# Revit family: CA-4_DWDI_ARR_3_CCW_BHD
name_source: partatom
category: Mechanical Equipment
units: mm (PartAtom-declared; Revit-internal decimal feet)

## family parameters
Always vertical = Yes
Cut with Voids When Loaded = No
Part Type = Normal
Room Calculation Point = No
Round Connector Dimension = Use Radius
Shared = No
Work Plane-Based = No

## types (54) — shared parameters
0 = 0"
1" = 1"
1.5 = 1 1/2"
2" = 2"
2' = 24"
3" = 3"
4" = 4"
Manufacturer = Loren Cook Company
ONE EIGTH = 1/8"
Type Comments = Airfoil Centrifugal Blower Arrangement 3 Counter-Clockwise Bottom Horizontal Discharge
URL = www.lorencook.com

## per-type parameters (varying)
- 120_CA-4_DWDI_ARR_3_CCW_BHD_CLASS_1: (B/2)+J=10 27/32"; (F/2)-S=3 7/8"; -(B/2)-J=-10 27/32"; -B=-17 11/16"; -B/2=-8 27/32"; -J*1.5=-3"; -L+M=-22 15/16"; -M=-5 3/4"; A=12 1/8"; A+.25"=12 3/8"; B=17 11/16"; B+.25"=17 15/16"; B/2=8 27/32"; BHD_E=10 3/4"; D=25 15/16"; D/2=12 31/32"; E=15 3/16"; E+(INLET_RAD+1.5")=24 13/16"; E-(INLET_RAD+1.5")=5 9/16"; F=22 3/4"; F/2=11 3/8"; F/8=2 27/32"; G=10 3/8"; H=2"; INLET_DIA=16 1/4"; INLET_RAD=8 1/8"; INLET_RAD+1.5"=9 5/8"; INLET_RAD/2=4 1/16"; J=2"; J*1.5=3"; J-.125"=1 7/8"; L=28 11/16"; M=5 3/4"; Model=CA-4 DWDI CCW BHD Class 1; N=1 7/16"; N*2=2 7/8"; N/2=23/32"; O=9 31/32"; P=19 15/16"; P/2=9 31/32"; S=7 1/2"; T=11/16"; T/2=11/32"
- 120_CA-4_DWDI_ARR_3_CCW_BHD_CLASS_2: (B/2)+J=10 27/32"; (F/2)-S=3 7/8"; -(B/2)-J=-10 27/32"; -B=-17 11/16"; -B/2=-8 27/32"; -J*1.5=-3"; -L+M=-23 5/16"; -M=-6 1/8"; A=12 1/8"; A+.25"=12 3/8"; B=17 11/16"; B+.25"=17 15/16"; B/2=8 27/32"; BHD_E=10 3/4"; D=25 15/16"; D/2=12 31/32"; E=15 3/16"; E+(INLET_RAD+1.5")=24 13/16"; E-(INLET_RAD+1.5")=5 9/16"; F=22 3/4"; F/2=11 3/8"; F/8=2 27/32"; G=10 3/8"; H=2"; INLET_DIA=16 1/4"; INLET_RAD=8 1/8"; INLET_RAD+1.5"=9 5/8"; INLET_RAD/2=4 1/16"; J=2"; J*1.5=3"; J-.125"=1 7/8"; L=29 7/16"; M=6 1/8"; Model=CA-4 DWDI CCW BHD Class 2; N=1 11/16"; N*2=3 3/8"; N/2=27/32"; O=9 31/32"; P=19 15/16"; P/2=9 31/32"; S=7 1/2"; T=11/16"; T/2=11/32"
- 120_CA-4_DWDI_ARR_3_CCW_BHD_CLASS_3: (B/2)+J=10 27/32"; (F/2)-S=3 7/8"; -(B/2)-J=-10 27/32"; -B=-17 11/16"; -B/2=-8 27/32"; -J*1.5=-3"; -L+M=-23 9/16"; -M=-6 3/8"; A=12 1/8"; A+.25"=12 3/8"; B=17 11/16"; B+.25"=17 15/16"; B/2=8 27/32"; BHD_E=10 3/4"; D=25 15/16"; D/2=12 31/32"; E=15 3/16"; E+(INLET_RAD+1.5")=24 13/16"; E-(INLET_RAD+1.5")=5 9/16"; F=22 3/4"; F/2=11 3/8"; F/8=2 27/32"; G=10 3/8"; H=2"; INLET_DIA=16 1/4"; INLET_RAD=8 1/8"; INLET_RAD+1.5"=9 5/8"; INLET_RAD/2=4 1/16"; J=2"; J*1.5=3"; J-.125"=1 7/8"; L=29 15/16"; M=6 3/8"; Model=CA-4 DWDI CCW BHD Class 3; N=1 15/16"; N*2=3 7/8"; N/2=31/32"; O=9 31/32"; P=19 15/16"; P/2=9 31/32"; S=7 1/2"; T=11/16"; T/2=11/32"
- 135_CA-4_DWDI_ARR_3_CCW_BHD_CLASS_1: (B/2)+J=11 31/32"; (F/2)-S=4 1/4"; -(B/2)-J=-11 31/32"; -B=-19 15/16"; -B/2=-9 31/32"; -J*1.5=-3"; -L+M=-25 3/16"; -M=-5 3/4"; A=13 5/8"; A+.25"=13 7/8"; B=19 15/16"; B+.25"=20 3/16"; B/2=9 31/32"; BHD_E=12"; D=28 13/16"; D/2=14 13/32"; E=16 13/16"; E+(INLET_RAD+1.5")=27 3/16"; E-(INLET_RAD+1.5")=6 7/16"; F=25 1/2"; F/2=12 3/4"; F/8=3 3/16"; G=11 5/8"; H=2"; INLET_DIA=17 3/4"; INLET_RAD=8 7/8"; INLET_RAD+1.5"=10 3/8"; INLET_RAD/2=4 7/16"; J=2"; J*1.5=3"; J-.125"=1 7/8"; L=30 15/16"; M=5 3/4"; Model=CA-4 DWDI CCW BHD Class 1; N=1 7/16"; N*2=2 7/8"; N/2=23/32"; O=11 3/32"; P=22 3/16"; P/2=11 3/32"; S=8 1/2"; T=11/16"; T/2=11/32"
- 135_CA-4_DWDI_ARR_3_CCW_BHD_CLASS_2: (B/2)+J=11 31/32"; (F/2)-S=4 1/4"; -(B/2)-J=-11 31/32"; -B=-19 15/16"; -B/2=-9 31/32"; -J*1.5=-3"; -L+M=-25 9/16"; -M=-6 1/8"; A=13 5/8"; A+.25"=13 7/8"; B=19 15/16"; B+.25"=20 3/16"; B/2=9 31/32"; BHD_E=12"; D=28 13/16"; D/2=14 13/32"; E=16 13/16"; E+(INLET_RAD+1.5")=27 3/16"; E-(INLET_RAD+1.5")=6 7/16"; F=25 1/2"; F/2=12 3/4"; F/8=3 3/16"; G=11 5/8"; H=2"; INLET_DIA=17 3/4"; INLET_RAD=8 7/8"; INLET_RAD+1.5"=10 3/8"; INLET_RAD/2=4 7/16"; J=2"; J*1.5=3"; J-.125"=1 7/8"; L=31 11/16"; M=6 1/8"; Model=CA-4 DWDI CCW BHD Class 2; N=1 11/16"; N*2=3 3/8"; N/2=27/32"; O=11 3/32"; P=22 3/16"; P/2=11 3/32"; S=8 1/2"; T=11/16"; T/2=11/32"
- 135_CA-4_DWDI_ARR_3_CCW_BHD_CLASS_3: (B/2)+J=11 31/32"; (F/2)-S=4 1/4"; -(B/2)-J=-11 31/32"; -B=-19 15/16"; -B/2=-9 31/32"; -J*1.5=-3"; -L+M=-26 1/16"; -M=-6 5/8"; A=13 5/8"; A+.25"=13 7/8"; B=19 15/16"; B+.25"=20 3/16"; B/2=9 31/32"; BHD_E=12"; D=28 13/16"; D/2=14 13/32"; E=16 13/16"; E+(INLET_RAD+1.5")=27 3/16"; E-(INLET_RAD+1.5")=6 7/16"; F=25 1/2"; F/2=12 3/4"; F/8=3 3/16"; G=11 5/8"; H=2"; INLET_DIA=17 3/4"; INLET_RAD=8 7/8"; INLET_RAD+1.5"=10 3/8"; INLET_RAD/2=4 7/16"; J=2"; J*1.5=3"; J-.125"=1 7/8"; L=32 11/16"; M=6 5/8"; Model=CA-4 DWDI CCW BHD Class 3; N=2 3/16"; N*2=4 3/8"; N/2=1 3/32"; O=11 3/32"; P=22 3/16"; P/2=11 3/32"; S=8 1/2"; T=11/16"; T/2=11/32"
- 150_CA-4_DWDI_ARR_3_CCW_BHD_CLASS_1: (B/2)+J=13"; (F/2)-S=5 1/16"; -(B/2)-J=-13"; -B=-22"; -B/2=-11"; -J*1.5=-3"; -L+M=-27 5/8"; -M=-6 5/8"; A=15 1/4"; A+.25"=15 1/2"; B=22"; B+.25"=22 1/4"; B/2=11"; BHD_E=13 1/4"; D=31 11/16"; D/2=15 27/32"; E=18 7/16"; E+(INLET_RAD+1.5")=29 9/16"; E-(INLET_RAD+1.5")=7 5/16"; F=28 1/8"; F/2=14 1/16"; F/8=3 17/32"; G=12 7/8"; H=2"; INLET_DIA=19 1/4"; INLET_RAD=9 5/8"; INLET_RAD+1.5"=11 1/8"; INLET_RAD/2=4 13/16"; J=2"; J*1.5=3"; J-.125"=1 7/8"; L=34 1/4"; M=6 5/8"; Model=CA-4 DWDI CCW BHD Class 1; N=1 11/16"; N*2=3 3/8"; N/2=27/32"; O=12 1/8"; P=24 1/4"; P/2=12 1/8"; S=9"; T=11/16"; T/2=11/32"
- 150_CA-4_DWDI_ARR_3_CCW_BHD_CLASS_2: (B/2)+J=13"; (F/2)-S=5 1/16"; -(B/2)-J=-13"; -B=-22"; -B/2=-11"; -J*1.5=-3"; -L+M=-27 7/8"; -M=-6 7/8"; A=15 1/4"; A+.25"=15 1/2"; B=22"; B+.25"=22 1/4"; B/2=11"; BHD_E=13 1/4"; D=31 11/16"; D/2=15 27/32"; E=18 7/16"; E+(INLET_RAD+1.5")=29 9/16"; E-(INLET_RAD+1.5")=7 5/16"; F=28 1/8"; F/2=14 1/16"; F/8=3 17/32"; G=12 7/8"; H=2"; INLET_DIA=19 1/4"; INLET_RAD=9 5/8"; INLET_RAD+1.5"=11 1/8"; INLET_RAD/2=4 13/16"; J=2"; J*1.5=3"; J-.125"=1 7/8"; L=34 3/4"; M=6 7/8"; Model=CA-4 DWDI CCW BHD Class 2; N=1 15/16"; N*2=3 7/8"; N/2=31/32"; O=12 1/8"; P=24 1/4"; P/2=12 1/8"; S=9"; T=11/16"; T/2=11/32"
- 150_CA-4_DWDI_ARR_3_CCW_BHD_CLASS_3: (B/2)+J=13"; (F/2)-S=5 1/16"; -(B/2)-J=-13"; -B=-22"; -B/2=-11"; -J*1.5=-3"; -L+M=-28 1/4"; -M=-7 1/4"; A=15 1/4"; A+.25"=15 1/2"; B=22"; B+.25"=22 1/4"; B/2=11"; BHD_E=13 1/4"; D=31 11/16"; D/2=15 27/32"; E=18 7/16"; E+(INLET_RAD+1.5")=29 9/16"; E-(INLET_RAD+1.5")=7 5/16"; F=28 1/8"; F/2=14 1/16"; F/8=3 17/32"; G=12 7/8"; H=2"; INLET_DIA=19 1/4"; INLET_RAD=9 5/8"; INLET_RAD+1.5"=11 1/8"; INLET_RAD/2=4 13/16"; J=2"; J*1.5=3"; J-.125"=1 7/8"; L=35 1/2"; M=7 1/4"; Model=CA-4 DWDI CCW BHD Class 3; N=2 7/16"; N*2=4 7/8"; N/2=1 7/32"; O=12 1/8"; P=24 1/4"; P/2=12 1/8"; S=9"; T=11/16"; T/2=11/32"
- 165_CA-4_DWDI_ARR_3_CCW_BHD_CLASS_1: (B/2)+J=14"; (F/2)-S=5 7/16"; -(B/2)-J=-14"; -B=-24"; -B/2=-12"; -J*1.5=-3"; -L+M=-29 5/8"; -M=-6 5/8"; A=16 15/16"; A+.25"=17 3/16"; B=24"; B+.25"=24 1/4"; B/2=12"; BHD_E=14 3/8"; D=34 7/16"; D/2=17 7/32"; E=20 1/16"; E+(INLET_RAD+1.5")=32 3/16"; E-(INLET_RAD+1.5")=7 15/16"; F=30 7/8"; F/2=15 7/16"; F/8=3 7/8"; G=14 1/4"; H=2"; INLET_DIA=21 1/4"; INLET_RAD=10 5/8"; INLET_RAD+1.5"=12 1/8"; INLET_RAD/2=5 5/16"; J=2"; J*1.5=3"; J-.125"=1 7/8"; L=36 1/4"; M=6 5/8"; Model=CA-4 DWDI CCW BHD Class 1; N=1 11/16"; N*2=3 3/8"; N/2=27/32"; O=13 1/8"; P=26 1/4"; P/2=13 1/8"; S=10"; T=11/16"; T/2=11/32"
- 165_CA-4_DWDI_ARR_3_CCW_BHD_CLASS_2: (B/2)+J=14"; (F/2)-S=5 7/16"; -(B/2)-J=-14"; -B=-24"; -B/2=-12"; -J*1.5=-3"; -L+M=-29 7/8"; -M=-6 7/8"; A=16 15/16"; A+.25"=17 3/16"; B=24"; B+.25"=24 1/4"; B/2=12"; BHD_E=14 3/8"; D=34 7/16"; D/2=17 7/32"; E=20 1/16"; E+(INLET_RAD+1.5")=32 3/16"; E-(INLET_RAD+1.5")=7 15/16"; F=30 7/8"; F/2=15 7/16"; F/8=3 7/8"; G=14 1/4"; H=2"; INLET_DIA=21 1/4"; INLET_RAD=10 5/8"; INLET_RAD+1.5"=12 1/8"; INLET_RAD/2=5 5/16"; J=2"; J*1.5=3"; J-.125"=1 7/8"; L=36 3/4"; M=6 7/8"; Model=CA-4 DWDI CCW BHD Class 2; N=1 15/16"; N*2=3 7/8"; N/2=31/32"; O=13 1/8"; P=26 1/4"; P/2=13 1/8"; S=10"; T=11/16"; T/2=11/32"
- 165_CA-4_DWDI_ARR_3_CCW_BHD_CLASS_3: (B/2)+J=14"; (F/2)-S=5 7/16"; -(B/2)-J=-14"; -B=-24"; -B/2=-12"; -J*1.5=-3"; -L+M=-30 5/16"; -M=-7 3/16"; A=16 15/16"; A+.25"=17 3/16"; B=24"; B+.25"=24 1/4"; B/2=12"; BHD_E=14 3/8"; D=34 7/16"; D/2=17 7/32"; E=20 1/16"; E+(INLET_RAD+1.5")=32 3/16"; E-(INLET_RAD+1.5")=7 15/16"; F=30 7/8"; F/2=15 7/16"; F/8=3 7/8"; G=14 1/4"; H=2"; INLET_DIA=21 1/4"; INLET_RAD=10 5/8"; INLET_RAD+1.5"=12 1/8"; INLET_RAD/2=5 5/16"; J=2"; J*1.5=3"; J-.125"=1 7/8"; L=37 1/2"; M=7 3/16"; Model=CA-4 DWDI CCW BHD Class 3; N=2 7/16"; N*2=4 7/8"; N/2=1 7/32"; O=13 1/8"; P=26 1/4"; P/2=13 1/8"; S=10"; T=11/16"; T/2=11/32"
- 180_CA-4_DWDI_ARR_3_CCW_BHD_CLASS_1: (B/2)+J=15 1/32"; (F/2)-S=5 13/16"; -(B/2)-J=-15 1/32"; -B=-26 1/16"; -B/2=-13 1/32"; -J*1.5=-3"; -L+M=-31 11/16"; -M=-7 1/8"; A=18 1/2"; A+.25"=18 3/4"; B=26 1/16"; B+.25"=26 5/16"; B/2=13 1/32"; BHD_E=15 5/8"; D=37 5/16"; D/2=18 21/32"; E=21 11/16"; E+(INLET_RAD+1.5")=34 9/16"; E-(INLET_RAD+1.5")=8 13/16"; F=33 5/8"; F/2=16 13/16"; F/8=4 7/32"; G=15 1/2"; H=2"; INLET_DIA=22 3/4"; INLET_RAD=11 3/8"; INLET_RAD+1.5"=12 7/8"; INLET_RAD/2=5 11/16"; J=2"; J*1.5=3"; J-.125"=1 7/8"; L=38 13/16"; M=7 1/8"; Model=CA-4 DWDI CCW BHD Class 1; N=1 11/16"; N*2=3 3/8"; N/2=27/32"; O=14 5/32"; P=28 5/16"; P/2=14 5/32"; S=11"; T=11/16"; T/2=11/32"
- 180_CA-4_DWDI_ARR_3_CCW_BHD_CLASS_2: (B/2)+J=15 1/32"; (F/2)-S=5 13/16"; -(B/2)-J=-15 1/32"; -B=-26 1/16"; -B/2=-13 1/32"; -J*1.5=-3"; -L+M=-31 15/16"; -M=-7 3/8"; A=18 1/2"; A+.25"=18 3/4"; B=26 1/16"; B+.25"=26 5/16"; B/2=13 1/32"; BHD_E=15 5/8"; D=37 5/16"; D/2=18 21/32"; E=21 11/16"; E+(INLET_RAD+1.5")=34 9/16"; E-(INLET_RAD+1.5")=8 13/16"; F=33 5/8"; F/2=16 13/16"; F/8=4 7/32"; G=15 1/2"; H=2"; INLET_DIA=22 3/4"; INLET_RAD=11 3/8"; INLET_RAD+1.5"=12 7/8"; INLET_RAD/2=5 11/16"; J=2"; J*1.5=3"; J-.125"=1 7/8"; L=39 5/16"; M=7 3/8"; Model=CA-4 DWDI CCW BHD Class 2; N=1 15/16"; N*2=3 7/8"; N/2=31/32"; O=14 5/32"; P=28 5/16"; P/2=14 5/32"; S=11"; T=11/16"; T/2=11/32"
- 180_CA-4_DWDI_ARR_3_CCW_BHD_CLASS_3: (B/2)+J=15 1/32"; (F/2)-S=5 13/16"; -(B/2)-J=-15 1/32"; -B=-26 1/16"; -B/2=-13 1/32"; -J*1.5=-3"; -L+M=-32 5/16"; -M=-7 3/4"; A=18 1/2"; A+.25"=18 3/4"; B=26 1/16"; B+.25"=26 5/16"; B/2=13 1/32"; BHD_E=15 5/8"; D=37 5/16"; D/2=18 21/32"; E=21 11/16"; E+(INLET_RAD+1.5")=34 9/16"; E-(INLET_RAD+1.5")=8 13/16"; F=33 5/8"; F/2=16 13/16"; F/8=4 7/32"; G=15 1/2"; H=2"; INLET_DIA=22 3/4"; INLET_RAD=11 3/8"; INLET_RAD+1.5"=12 7/8"; INLET_RAD/2=5 11/16"; J=2"; J*1.5=3"; J-.125"=1 7/8"; L=40 1/16"; M=7 3/4"; Model=CA-4 DWDI CCW BHD Class 3; N=2 7/16"; N*2=4 7/8"; N/2=1 7/32"; O=14 5/32"; P=28 5/16"; P/2=14 5/32"; S=11"; T=11/16"; T/2=11/32"
- 195_CA-4_DWDI_ARR_3_CCW_BHD_CLASS_1: (B/2)+J=16 7/32"; (F/2)-S=6 5/8"; -(B/2)-J=-16 7/32"; -B=-28 7/16"; -B/2=-14 7/32"; -J*1.5=-3"; -L+M=-34 7/16"; -M=-7 1/4"; A=19 1/2"; A+.25"=19 3/4"; B=28 7/16"; B+.25"=28 11/16"; B/2=14 7/32"; BHD_E=16 3/4"; D=40 1/16"; D/2=20 1/32"; E=23 5/16"; E+(INLET_RAD+1.5")=36 15/16"; E-(INLET_RAD+1.5")=9 11/16"; F=36 1/4"; F/2=18 1/8"; F/8=4 17/32"; G=16 3/4"; H=2"; INLET_DIA=24 1/4"; INLET_RAD=12 1/8"; INLET_RAD+1.5"=13 5/8"; INLET_RAD/2=6 1/16"; J=2"; J*1.5=3"; J-.125"=1 7/8"; L=41 11/16"; M=7 1/4"; Model=CA-4 DWDI CCW BHD Class 1; N=1 15/16"; N*2=3 7/8"; N/2=31/32"; O=15 11/32"; P=30 11/16"; P/2=15 11/32"; S=11 1/2"; T=11/16"; T/2=11/32"
- 195_CA-4_DWDI_ARR_3_CCW_BHD_CLASS_2: (B/2)+J=16 7/32"; (F/2)-S=6 5/8"; -(B/2)-J=-16 7/32"; -B=-28 7/16"; -B/2=-14 7/32"; -J*1.5=-3"; -L+M=-34 9/16"; -M=-7 5/8"; A=19 1/2"; A+.25"=19 3/4"; B=28 7/16"; B+.25"=28 11/16"; B/2=14 7/32"; BHD_E=16 3/4"; D=40 1/16"; D/2=20 1/32"; E=23 5/16"; E+(INLET_RAD+1.5")=36 15/16"; E-(INLET_RAD+1.5")=9 11/16"; F=36 1/4"; F/2=18 1/8"; F/8=4 17/32"; G=16 3/4"; H=2"; INLET_DIA=24 1/4"; INLET_RAD=12 1/8"; INLET_RAD+1.5"=13 5/8"; INLET_RAD/2=6 1/16"; J=2"; J*1.5=3"; J-.125"=1 7/8"; L=42 3/16"; M=7 5/8"; Model=CA-4 DWDI CCW BHD Class 2; N=2 3/16"; N*2=4 3/8"; N/2=1 3/32"; O=15 11/32"; P=30 11/16"; P/2=15 11/32"; S=11 1/2"; T=11/16"; T/2=11/32"
- 195_CA-4_DWDI_ARR_3_CCW_BHD_CLASS_3: (B/2)+J=16 7/32"; (F/2)-S=6 5/8"; -(B/2)-J=-16 7/32"; -B=-28 7/16"; -B/2=-14 7/32"; -J*1.5=-3"; -L+M=-34 15/16"; -M=-8"; A=19 1/2"; A+.25"=19 3/4"; B=28 7/16"; B+.25"=28 11/16"; B/2=14 7/32"; BHD_E=16 3/4"; D=40 1/16"; D/2=20 1/32"; E=23 5/16"; E+(INLET_RAD+1.5")=36 15/16"; E-(INLET_RAD+1.5")=9 11/16"; F=36 1/4"; F/2=18 1/8"; F/8=4 17/32"; G=16 3/4"; H=2"; INLET_DIA=24 1/4"; INLET_RAD=12 1/8"; INLET_RAD+1.5"=13 5/8"; INLET_RAD/2=6 1/16"; J=2"; J*1.5=3"; J-.125"=1 7/8"; L=42 15/16"; M=8"; Model=CA-4 DWDI CCW BHD Class 3; N=2 11/16"; N*2=5 3/8"; N/2=1 11/32"; O=15 11/32"; P=30 11/16"; P/2=15 11/32"; S=11 1/2"; T=11/16"; T/2=11/32"
- 210_CA-4_DWDI_ARR_3_CCW_BHD_CLASS_1: (B/2)+J=17 3/16"; (F/2)-S=7 9/16"; -(B/2)-J=-17 3/16"; -B=-30 3/8"; -B/2=-15 3/16"; -J*1.5=-3"; -L+M=-36 1/4"; -M=-7 7/8"; A=21 5/8"; A+.25"=21 7/8"; B=30 3/8"; B+.25"=30 5/8"; B/2=15 3/16"; BHD_E=18"; D=42 15/16"; D/2=21 15/32"; E=24 15/16"; E+(INLET_RAD+1.5")=39 7/16"; E-(INLET_RAD+1.5")=10 7/16"; F=39 1/8"; F/2=19 9/16"; F/8=4 29/32"; G=18 1/8"; H=2"; INLET_DIA=26"; INLET_RAD=13"; INLET_RAD+1.5"=14 1/2"; INLET_RAD/2=6 1/2"; J=2"; J*1.5=3"; J-.125"=1 7/8"; L=44 1/8"; M=7 7/8"; Model=CA-4 DWDI CCW BHD Class 1; N=1 15/16"; N*2=3 7/8"; N/2=31/32"; O=6 5/16"; P=32 5/8"; P/2=16 5/16"; S=12"; T=15/16"; T/2=15/32"
- 210_CA-4_DWDI_ARR_3_CCW_BHD_CLASS_2: (B/2)+J=17 3/16"; (F/2)-S=7 9/16"; -(B/2)-J=-17 3/16"; -B=-30 3/8"; -B/2=-15 3/16"; -J*1.5=-3"; -L+M=-36 1/2"; -M=-8 1/8"; A=21 5/8"; A+.25"=21 7/8"; B=30 3/8"; B+.25"=30 5/8"; B/2=15 3/16"; BHD_E=18"; D=42 15/16"; D/2=21 15/32"; E=24 15/16"; E+(INLET_RAD+1.5")=39 7/16"; E-(INLET_RAD+1.5")=10 7/16"; F=39 1/8"; F/2=19 9/16"; F/8=4 29/32"; G=18 1/8"; H=2"; INLET_DIA=26"; INLET_RAD=13"; INLET_RAD+1.5"=14 1/2"; INLET_RAD/2=6 1/2"; J=2"; J*1.5=3"; J-.125"=1 7/8"; L=44 5/8"; M=8 1/8"; Model=CA-4 DWDI CCW BHD Class 2; N=2 3/16"; N*2=4 3/8"; N/2=1 3/32"; O=6 5/16"; P=32 5/8"; P/2=16 5/16"; S=12"; T=15/16"; T/2=15/32"
- 210_CA-4_DWDI_ARR_3_CCW_BHD_CLASS_3: (B/2)+J=17 3/16"; (F/2)-S=7 9/16"; -(B/2)-J=-17 3/16"; -B=-30 3/8"; -B/2=-15 3/16"; -J*1.5=-3"; -L+M=-36 7/8"; -M=-8 1/2"; A=21 5/8"; A+.25"=21 7/8"; B=30 3/8"; B+.25"=30 5/8"; B/2=15 3/16"; BHD_E=18"; D=42 15/16"; D/2=21 15/32"; E=24 15/16"; E+(INLET_RAD+1.5")=39 7/16"; E-(INLET_RAD+1.5")=10 7/16"; F=39 1/8"; F/2=19 9/16"; F/8=4 29/32"; G=18 1/8"; H=2"; INLET_DIA=26"; INLET_RAD=13"; INLET_RAD+1.5"=14 1/2"; INLET_RAD/2=6 1/2"; J=2"; J*1.5=3"; J-.125"=1 7/8"; L=45 3/8"; M=8 1/2"; Model=CA-4 DWDI CCW BHD Class 3; N=2 11/16"; N*2=5 3/8"; N/2=1 11/32"; O=6 5/16"; P=32 5/8"; P/2=16 5/16"; S=12"; T=15/16"; T/2=15/32"
- 225_CA-4_DWDI_ARR_3_CCW_BHD_CLASS_1: (B/2)+J=18 1/4"; (F/2)-S=8 3/8"; -(B/2)-J=-18 1/4"; -B=-32 1/2"; -B/2=-16 1/4"; -J*1.5=-3"; -L+M=-38 3/8"; -M=-7 7/8"; A=23 3/16"; A+.25"=23 7/16"; B=32 1/2"; B+.25"=32 3/4"; B/2=16 1/4"; BHD_E=19 1/4"; D=45 13/16"; D/2=22 29/32"; E=26 9/16"; E+(INLET_RAD+1.5")=41 13/16"; E-(INLET_RAD+1.5")=11 5/16"; F=41 3/4"; F/2=20 7/8"; F/8=5 7/32"; G=19 3/8"; H=2"; INLET_DIA=27 1/2"; INLET_RAD=13 3/4"; INLET_RAD+1.5"=15 1/4"; INLET_RAD/2=6 7/8"; J=2"; J*1.5=3"; J-.125"=1 7/8"; L=46 1/4"; M=7 7/8"; Model=CA-4 DWDI CCW BHD Class 1; N=1 15/16"; N*2=3 7/8"; N/2=31/32"; O=17 3/8"; P=34 3/4"; P/2=17 3/8"; S=12 1/2"; T=15/16"; T/2=15/32"
- 225_CA-4_DWDI_ARR_3_CCW_BHD_CLASS_2: (B/2)+J=18 1/4"; (F/2)-S=8 3/8"; -(B/2)-J=-18 1/4"; -B=-32 1/2"; -B/2=-16 1/4"; -J*1.5=-3"; -L+M=-38 3/4"; -M=-8 1/4"; A=23 3/16"; A+.25"=23 7/16"; B=32 1/2"; B+.25"=32 3/4"; B/2=16 1/4"; BHD_E=19 1/4"; D=45 13/16"; D/2=22 29/32"; E=26 9/16"; E+(INLET_RAD+1.5")=41 13/16"; E-(INLET_RAD+1.5")=11 5/16"; F=41 3/4"; F/2=20 7/8"; F/8=5 7/32"; G=19 3/8"; H=2"; INLET_DIA=27 1/2"; INLET_RAD=13 3/4"; INLET_RAD+1.5"=15 1/4"; INLET_RAD/2=6 7/8"; J=2"; J*1.5=3"; J-.125"=1 7/8"; L=47"; M=8 1/4"; Model=CA-4 DWDI CCW BHD Class 2; N=2 7/16"; N*2=4 7/8"; N/2=1 7/32"; O=17 3/8"; P=34 3/4"; P/2=17 3/8"; S=12 1/2"; T=15/16"; T/2=15/32"
- 225_CA-4_DWDI_ARR_3_CCW_BHD_CLASS_3: (B/2)+J=18 1/4"; (F/2)-S=8 3/8"; -(B/2)-J=-18 1/4"; -B=-32 1/2"; -B/2=-16 1/4"; -J*1.5=-3"; -L+M=-39"; -M=-8 1/2"; A=23 3/16"; A+.25"=23 7/16"; B=32 1/2"; B+.25"=32 3/4"; B/2=16 1/4"; BHD_E=19 1/4"; D=45 13/16"; D/2=22 29/32"; E=26 9/16"; E+(INLET_RAD+1.5")=41 13/16"; E-(INLET_RAD+1.5")=11 5/16"; F=41 3/4"; F/2=20 7/8"; F/8=5 7/32"; G=19 3/8"; H=2"; INLET_DIA=27 1/2"; INLET_RAD=13 3/4"; INLET_RAD+1.5"=15 1/4"; INLET_RAD/2=6 7/8"; J=2"; J*1.5=3"; J-.125"=1 7/8"; L=47 1/2"; M=8 1/2"; Model=CA-4 DWDI CCW BHD Class 3; N=2 15/16"; N*2=5 7/8"; N/2=1 15/32"; O=17 3/8"; P=34 3/4"; P/2=17 3/8"; S=12 1/2"; T=15/16"; T/2=15/32"
- 245_CA-4_DWDI_ARR_3_CCW_BHD_CLASS_1: (B/2)+J=19 17/32"; (F/2)-S=10 3/16"; -(B/2)-J=-19 17/32"; -B=-35 1/16"; -B/2=-17 17/32"; -J*1.5=-3"; -L+M=-41 3/16"; -M=-8 5/8"; A=25 1/2"; A+.25"=25 3/4"; B=35 1/16"; B+.25"=35 5/16"; B/2=17 17/32"; BHD_E=20 7/8"; D=49 5/8"; D/2=24 13/16"; E=28 3/4"; E+(INLET_RAD+1.5")=45"; E-(INLET_RAD+1.5")=12 1/2"; F=45 3/8"; F/2=22 11/16"; F/8=5 11/16"; G=21 1/8"; H=2"; INLET_DIA=29 1/2"; INLET_RAD=14 3/4"; INLET_RAD+1.5"=16 1/4"; INLET_RAD/2=7 3/8"; J=2"; J*1.5=3"; J-.125"=1 7/8"; L=49 13/16"; M=8 5/8"; Model=CA-4 DWDI CCW BHD Class 1; N=2 3/16"; N*2=4 3/8"; N/2=1 3/32"; O=18 21/32"; P=37 5/16"; P/2=18 21/32"; S=12 1/2"; T=15/16"; T/2=15/32"
- 245_CA-4_DWDI_ARR_3_CCW_BHD_CLASS_2: (B/2)+J=19 17/32"; (F/2)-S=10 3/16"; -(B/2)-J=-19 17/32"; -B=-35 1/16"; -B/2=-17 17/32"; -J*1.5=-3"; -L+M=-41 5/16"; -M=-8 3/4"; A=25 1/2"; A+.25"=25 3/4"; B=35 1/16"; B+.25"=35 5/16"; B/2=17 17/32"; BHD_E=20 7/8"; D=49 5/8"; D/2=24 13/16"; E=28 3/4"; E+(INLET_RAD+1.5")=45"; E-(INLET_RAD+1.5")=12 1/2"; F=45 3/8"; F/2=22 11/16"; F/8=5 11/16"; G=21 1/8"; H=2"; INLET_DIA=29 1/2"; INLET_RAD=14 3/4"; INLET_RAD+1.5"=16 1/4"; INLET_RAD/2=7 3/8"; J=2"; J*1.5=3"; J-.125"=1 7/8"; L=50 1/16"; M=8 3/4"; Model=CA-4 DWDI CCW BHD Class 2; N=2 7/16"; N*2=4 7/8"; N/2=1 7/32"; O=18 21/32"; P=37 5/16"; P/2=18 21/32"; S=12 1/2"; T=15/16"; T/2=15/32"
- 245_CA-4_DWDI_ARR_3_CCW_BHD_CLASS_3: (B/2)+J=19 17/32"; (F/2)-S=10 3/16"; -(B/2)-J=-19 17/32"; -B=-35 1/16"; -B/2=-17 17/32"; -J*1.5=-3"; -L+M=-41 15/16"; -M=-8 3/4"; A=25 1/2"; A+.25"=25 3/4"; B=35 1/16"; B+.25"=35 5/16"; B/2=17 17/32"; BHD_E=20 7/8"; D=49 5/8"; D/2=24 13/16"; E=28 3/4"; E+(INLET_RAD+1.5")=45"; E-(INLET_RAD+1.5")=12 1/2"; F=45 3/8"; F/2=22 11/16"; F/8=5 11/16"; G=21 1/8"; H=2"; INLET_DIA=29 1/2"; INLET_RAD=14 3/4"; INLET_RAD+1.5"=16 1/4"; INLET_RAD/2=7 3/8"; J=2"; J*1.5=3"; J-.125"=1 7/8"; L=50 11/16"; M=8 3/4"; Model=CA-4 DWDI CCW BHD Class 3; N=2 3/16"; N*2=4 3/8"; N/2=1 3/32"; O=18 21/32"; P=37 5/16"; P/2=18 21/32"; S=12 1/2"; T=15/16"; T/2=15/32"
- 270_CA-4_DWDI_ARR_3_CCW_BHD_CLASS_1: (B/2)+J=21 23/32"; (F/2)-S=9 15/16"; -(B/2)-J=-21 23/32"; -B=-39 7/16"; -B/2=-19 23/32"; -J*1.5=-3"; -L+M=-45 9/16"; -M=-8 5/8"; A=27 1/2"; A+.25"=27 3/4"; B=39 7/16"; B+.25"=39 11/16"; B/2=19 23/32"; BHD_E=23 3/8"; D=54 7/8"; D/2=27 7/16"; E=31 1/2"; E+(INLET_RAD+1.5")=49"; E-(INLET_RAD+1.5")=14"; F=49 7/8"; F/2=24 15/16"; F/8=6 1/4"; G=23 1/4"; H=2"; INLET_DIA=32"; INLET_RAD=16"; INLET_RAD+1.5"=17 1/2"; INLET_RAD/2=8"; J=2"; J*1.5=3"; J-.125"=1 7/8"; L=54 3/16"; M=8 5/8"; Model=CA-4 DWDI CCW BHD Class 1; N=2 3/16"; N*2=4 3/8"; N/2=1 3/32"; O=20 27/32"; P=41 11/16"; P/2=20 27/32"; S=15"; T=15/16"; T/2=15/32"
- 270_CA-4_DWDI_ARR_3_CCW_BHD_CLASS_2: (B/2)+J=21 23/32"; (F/2)-S=9 15/16"; -(B/2)-J=-21 23/32"; -B=-39 7/16"; -B/2=-19 23/32"; -J*1.5=-3"; -L+M=-45 15/16"; -M=-9"; A=27 1/2"; A+.25"=27 3/4"; B=39 7/16"; B+.25"=39 11/16"; B/2=19 23/32"; BHD_E=23 3/8"; D=54 7/8"; D/2=27 7/16"; E=31 1/2"; E+(INLET_RAD+1.5")=49"; E-(INLET_RAD+1.5")=14"; F=49 7/8"; F/2=24 15/16"; F/8=6 1/4"; G=23 1/4"; H=2"; INLET_DIA=32"; INLET_RAD=16"; INLET_RAD+1.5"=17 1/2"; INLET_RAD/2=8"; J=2"; J*1.5=3"; J-.125"=1 7/8"; L=54 15/16"; M=9"; Model=CA-4 DWDI CCW BHD Class 2; N=2 11/16"; N*2=5 3/8"; N/2=1 11/32"; O=20 27/32"; P=41 11/16"; P/2=20 27/32"; S=15"; T=15/16"; T/2=15/32"
- 270_CA-4_DWDI_ARR_3_CCW_BHD_CLASS_3: (B/2)+J=21 23/32"; (F/2)-S=9 15/16"; -(B/2)-J=-21 23/32"; -B=-39 7/16"; -B/2=-19 23/32"; -J*1.5=-3"; -L+M=-46 5/16"; -M=-8 3/4"; A=27 1/2"; A+.25"=27 3/4"; B=39 7/16"; B+.25"=39 11/16"; B/2=19 23/32"; BHD_E=23 3/8"; D=54 7/8"; D/2=27 7/16"; E=31 1/2"; E+(INLET_RAD+1.5")=49"; E-(INLET_RAD+1.5")=14"; F=49 7/8"; F/2=24 15/16"; F/8=6 1/4"; G=23 1/4"; H=2"; INLET_DIA=32"; INLET_RAD=16"; INLET_RAD+1.5"=17 1/2"; INLET_RAD/2=8"; J=2"; J*1.5=3"; J-.125"=1 7/8"; L=55 1/16"; M=8 3/4"; Model=CA-4 DWDI CCW BHD Class 3; N=2 3/16"; N*2=4 3/8"; N/2=1 3/32"; O=20 27/32"; P=41 11/16"; P/2=20 27/32"; S=15"; T=15/16"; T/2=15/32"
- 300_CA-4_DWDI_ARR_3_CCW_BHD_CLASS_1: (B/2)+J=23 1/2"; (F/2)-S=11 3/16"; -(B/2)-J=-23 1/2"; -B=-43"; -B/2=-21 1/2"; -J*1.5=-3"; -L+M=-49 1/4"; -M=-9 1/4"; A=31 3/16"; A+.25"=31 7/16"; B=43"; B+.25"=43 1/4"; B/2=21 1/2"; BHD_E=25 3/8"; D=60 1/8"; D/2=30 1/16"; E=34 3/4"; E+(INLET_RAD+1.5")=53 3/4"; E-(INLET_RAD+1.5")=15 3/4"; F=55 3/8"; F/2=27 11/16"; F/8=6 15/16"; G=25 7/8"; H=2"; INLET_DIA=35"; INLET_RAD=17 1/2"; INLET_RAD+1.5"=19"; INLET_RAD/2=8 3/4"; J=2"; J*1.5=3"; J-.125"=1 7/8"; L=58 1/2"; M=9 1/4"; Model=CA-4 DWDI CCW BHD Class 1; N=2 7/16"; N*2=4 7/8"; N/2=1 7/32"; O=22 5/8"; P=45 1/4"; P/2=22 5/8"; S=16 1/2"; T=15/16"; T/2=15/32"
- 300_CA-4_DWDI_ARR_3_CCW_BHD_CLASS_2: (B/2)+J=23 1/2"; (F/2)-S=11 3/16"; -(B/2)-J=-23 1/2"; -B=-43"; -B/2=-21 1/2"; -J*1.5=-3"; -L+M=-49 1/2"; -M=-9 1/2"; A=31 3/16"; A+.25"=31 7/16"; B=43"; B+.25"=43 1/4"; B/2=21 1/2"; BHD_E=25 3/8"; D=60 1/8"; D/2=30 1/16"; E=34 3/4"; E+(INLET_RAD+1.5")=53 3/4"; E-(INLET_RAD+1.5")=15 3/4"; F=55 3/8"; F/2=27 11/16"; F/8=6 15/16"; G=25 7/8"; H=2"; INLET_DIA=35"; INLET_RAD=17 1/2"; INLET_RAD+1.5"=19"; INLET_RAD/2=8 3/4"; J=2"; J*1.5=3"; J-.125"=1 7/8"; L=59"; M=9 1/2"; Model=CA-4 DWDI CCW BHD Class 2; N=2 11/16"; N*2=5 3/8"; N/2=1 11/32"; O=22 5/8"; P=45 1/4"; P/2=22 5/8"; S=16 1/2"; T=15/16"; T/2=15/32"
- 300_CA-4_DWDI_ARR_3_CCW_BHD_CLASS_3: (B/2)+J=23 1/2"; (F/2)-S=11 3/16"; -(B/2)-J=-23 1/2"; -B=-43"; -B/2=-21 1/2"; -J*1.5=-3"; -L+M=-49 7/8"; -M=-9 1/2"; A=31 3/16"; A+.25"=31 7/16"; B=43"; B+.25"=43 1/4"; B/2=21 1/2"; BHD_E=25 3/8"; D=60 1/8"; D/2=30 1/16"; E=34 3/4"; E+(INLET_RAD+1.5")=53 3/4"; E-(INLET_RAD+1.5")=15 3/4"; F=55 3/8"; F/2=27 11/16"; F/8=6 15/16"; G=25 7/8"; H=2"; INLET_DIA=35"; INLET_RAD=17 1/2"; INLET_RAD+1.5"=19"; INLET_RAD/2=8 3/4"; J=2"; J*1.5=3"; J-.125"=1 7/8"; L=59 3/8"; M=9 1/2"; Model=CA-4 DWDI CCW BHD Class 3; N=2 7/16"; N*2=4 7/8"; N/2=1 7/32"; O=22 5/8"; P=45 1/4"; P/2=22 5/8"; S=16 1/2"; T=15/16"; T/2=15/32"
- 330_CA-4_DWDI_ARR_3_CCW_BHD_CLASS_1: (B/2)+J=25 17/32"; (F/2)-S=12 3/8"; -(B/2)-J=-25 17/32"; -B=-47 1/16"; -B/2=-23 17/32"; -J*1.5=-3"; -L+M=-53 1/2"; -M=-10 1/16"; A=34 1/2"; A+.25"=34 3/4"; B=47 1/16"; B+.25"=47 5/16"; B/2=23 17/32"; BHD_E=27 7/8"; D=65 15/16"; D/2=32 31/32"; E=38 1/16"; E+(INLET_RAD+1.5")=58 9/16"; E-(INLET_RAD+1.5")=17 9/16"; F=60 3/4"; F/2=30 3/8"; F/8=7 19/32"; G=28 3/8"; H=2"; INLET_DIA=38"; INLET_RAD=19"; INLET_RAD+1.5"=20 1/2"; INLET_RAD/2=9 1/2"; J=2"; J*1.5=3"; J-.125"=1 7/8"; L=63 9/16"; M=10 1/16"; Model=CA-4 DWDI CCW BHD Class 1; N=2 11/16"; N*2=5 3/8"; N/2=1 11/32"; O=24 21/32"; P=49 5/16"; P/2=24 21/32"; S=18"; T=15/16"; T/2=15/32"
- 330_CA-4_DWDI_ARR_3_CCW_BHD_CLASS_2: (B/2)+J=25 17/32"; (F/2)-S=12 3/8"; -(B/2)-J=-25 17/32"; -B=-47 1/16"; -B/2=-23 17/32"; -J*1.5=-3"; -L+M=-54 1/16"; -M=-9 5/8"; A=34 1/2"; A+.25"=34 3/4"; B=47 1/16"; B+.25"=47 5/16"; B/2=23 17/32"; BHD_E=27 7/8"; D=65 15/16"; D/2=32 31/32"; E=38 1/16"; E+(INLET_RAD+1.5")=58 9/16"; E-(INLET_RAD+1.5")=17 9/16"; F=60 3/4"; F/2=30 3/8"; F/8=7 19/32"; G=28 3/8"; H=2"; INLET_DIA=38"; INLET_RAD=19"; INLET_RAD+1.5"=20 1/2"; INLET_RAD/2=9 1/2"; J=2"; J*1.5=3"; J-.125"=1 7/8"; L=63 11/16"; M=9 5/8"; Model=CA-4 DWDI CCW BHD Class 2; N=2 3/16"; N*2=4 3/8"; N/2=1 3/32"; O=24 21/32"; P=49 5/16"; P/2=24 21/32"; S=18"; T=15/16"; T/2=15/32"
- 330_CA-4_DWDI_ARR_3_CCW_BHD_CLASS_3: (B/2)+J=25 17/32"; (F/2)-S=12 3/8"; -(B/2)-J=-25 17/32"; -B=-47 1/16"; -B/2=-23 17/32"; -J*1.5=-3"; -L+M=-53 15/16"; -M=-10"; A=34 1/2"; A+.25"=34 3/4"; B=47 1/16"; B+.25"=47 5/16"; B/2=23 17/32"; BHD_E=27 7/8"; D=65 15/16"; D/2=32 31/32"; E=38 1/16"; E+(INLET_RAD+1.5")=58 9/16"; E-(INLET_RAD+1.5")=17 9/16"; F=60 3/4"; F/2=30 3/8"; F/8=7 19/32"; G=28 3/8"; H=2"; INLET_DIA=38"; INLET_RAD=19"; INLET_RAD+1.5"=20 1/2"; INLET_RAD/2=9 1/2"; J=2"; J*1.5=3"; J-.125"=1 7/8"; L=63 15/16"; M=10"; Model=CA-4 DWDI CCW BHD Class 3; N=2 7/16"; N*2=4 7/8"; N/2=1 7/32"; O=24 21/32"; P=49 5/16"; P/2=24 21/32"; S=18"; T=15/16"; T/2=15/32"
- 365_CA-4_DWDI_ARR_3_CCW_BHD_CLASS_1: (B/2)+J=28 3/32"; (F/2)-S=13 1/2"; -(B/2)-J=-28 3/32"; -B=-52 3/16"; -B/2=-26 3/32"; -J*1.5=-3"; -L+M=-59"; -M=-10 5/16"; A=38 11/16"; A+.25"=38 15/16"; B=52 3/16"; B+.25"=52 7/16"; B/2=26 3/32"; BHD_E=30 5/8"; D=72 1/2"; D/2=36 1/4"; E=41 7/8"; E+(INLET_RAD+1.5")=64 1/8"; E-(INLET_RAD+1.5")=19 5/8"; F=67"; F/2=33 1/2"; F/8=8 3/8"; G=31 3/8"; H=2"; INLET_DIA=41 1/2"; INLET_RAD=20 3/4"; INLET_RAD+1.5"=22 1/4"; INLET_RAD/2=10 3/8"; J=2"; J*1.5=3"; J-.125"=1 7/8"; L=69 5/16"; M=10 5/16"; Model=CA-4 DWDI CCW BHD Class 1; N=2 3/16"; N*2=4 3/8"; N/2=1 3/32"; O=27 7/32"; P=54 7/16"; P/2=27 7/32"; S=20"; T=15/16"; T/2=15/32"
- 365_CA-4_DWDI_ARR_3_CCW_BHD_CLASS_2: (B/2)+J=28 3/32"; (F/2)-S=13 1/2"; -(B/2)-J=-28 3/32"; -B=-52 3/16"; -B/2=-26 3/32"; -J*1.5=-3"; -L+M=-59 1/16"; -M=-10 1/2"; A=38 11/16"; A+.25"=38 15/16"; B=52 3/16"; B+.25"=52 7/16"; B/2=26 3/32"; BHD_E=30 5/8"; D=72 1/2"; D/2=36 1/4"; E=41 7/8"; E+(INLET_RAD+1.5")=64 1/8"; E-(INLET_RAD+1.5")=19 5/8"; F=67"; F/2=33 1/2"; F/8=8 3/8"; G=31 3/8"; H=2"; INLET_DIA=41 1/2"; INLET_RAD=20 3/4"; INLET_RAD+1.5"=22 1/4"; INLET_RAD/2=10 3/8"; J=2"; J*1.5=3"; J-.125"=1 7/8"; L=69 9/16"; M=10 1/2"; Model=CA-4 DWDI CCW BHD Class 2; N=2 7/16"; N*2=4 7/8"; N/2=1 7/32"; O=27 7/32"; P=54 7/16"; P/2=27 7/32"; S=20"; T=15/16"; T/2=15/32"
- 365_CA-4_DWDI_ARR_3_CCW_BHD_CLASS_3: (B/2)+J=28 3/32"; (F/2)-S=13 1/2"; -(B/2)-J=-28 3/32"; -B=-52 3/16"; -B/2=-26 3/32"; -J*1.5=-3"; -L+M=-59 9/16"; -M=-10 1/2"; A=38 11/16"; A+.25"=38 15/16"; B=52 3/16"; B+.25"=52 7/16"; B/2=26 3/32"; BHD_E=30 5/8"; D=72 1/2"; D/2=36 1/4"; E=41 7/8"; E+(INLET_RAD+1.5")=64 1/8"; E-(INLET_RAD+1.5")=19 5/8"; F=67"; F/2=33 1/2"; F/8=8 3/8"; G=31 3/8"; H=2"; INLET_DIA=41 1/2"; INLET_RAD=20 3/4"; INLET_RAD+1.5"=22 1/4"; INLET_RAD/2=10 3/8"; J=2"; J*1.5=3"; J-.125"=1 7/8"; L=70 1/16"; M=10 1/2"; Model=CA-4 DWDI CCW BHD Class 3; N=2 11/16"; N*2=5 3/8"; N/2=1 11/32"; O=27 7/32"; P=54 7/16"; P/2=27 7/32"; S=20"; T=15/16"; T/2=15/32"
- 402_CA-4_DWDI_ARR_3_CCW_BHD_CLASS_1: (B/2)+J=31 29/32"; (F/2)-S=14 15/16"; -(B/2)-J=-31 29/32"; -B=-57 13/16"; -B/2=-28 29/32"; -J*1.5=-4 1/2"; -L+M=-65 11/16"; -M=-10"; A=41 3/4"; A+.25"=42"; B=57 13/16"; B+.25"=58 1/16"; B/2=28 29/32"; BHD_E=33 5/8"; D=80 9/16"; D/2=40 9/32"; E=46 15/16"; E+(INLET_RAD+1.5")=71 1/16"; E-(INLET_RAD+1.5")=22 13/16"; F=73 7/8"; F/2=36 15/16"; F/8=9 1/4"; G=34 5/8"; H=3"; INLET_DIA=45 1/4"; INLET_RAD=22 5/8"; INLET_RAD+1.5"=24 1/8"; INLET_RAD/2=11 5/16"; J=3"; J*1.5=4 1/2"; J-.125"=2 7/8"; L=75 11/16"; M=10"; Model=CA-4 DWDI CCW BHD Class 1; N=2 7/16"; N*2=4 7/8"; N/2=1 7/32"; O=30 21/32"; P=61 5/16"; P/2=30 21/32"; S=22"; T=1 1/16"; T/2=17/32"
- 402_CA-4_DWDI_ARR_3_CCW_BHD_CLASS_2: (B/2)+J=31 29/32"; (F/2)-S=14 15/16"; -(B/2)-J=-31 29/32"; -B=-57 13/16"; -B/2=-28 29/32"; -J*1.5=-4 1/2"; -L+M=-65 11/16"; -M=-10"; A=41 3/4"; A+.25"=42"; B=57 13/16"; B+.25"=58 1/16"; B/2=28 29/32"; BHD_E=33 5/8"; D=80 9/16"; D/2=40 9/32"; E=46 15/16"; E+(INLET_RAD+1.5")=71 1/16"; E-(INLET_RAD+1.5")=22 13/16"; F=73 7/8"; F/2=36 15/16"; F/8=9 1/4"; G=34 5/8"; H=3"; INLET_DIA=45 1/4"; INLET_RAD=22 5/8"; INLET_RAD+1.5"=24 1/8"; INLET_RAD/2=11 5/16"; J=3"; J*1.5=4 1/2"; J-.125"=2 7/8"; L=75 11/16"; M=10"; Model=CA-4 DWDI CCW BHD Class 2; N=2 7/16"; N*2=4 7/8"; N/2=1 7/32"; O=30 21/32"; P=61 5/16"; P/2=30 21/32"; S=22"; T=1 1/16"; T/2=17/32"
- 402_CA-4_DWDI_ARR_3_CCW_BHD_CLASS_3: (B/2)+J=31 29/32"; (F/2)-S=14 15/16"; -(B/2)-J=-31 29/32"; -B=-57 13/16"; -B/2=-28 29/32"; -J*1.5=-4 1/2"; -L+M=-65 11/16"; -M=-10 1/2"; A=41 3/4"; A+.25"=42"; B=57 13/16"; B+.25"=58 1/16"; B/2=28 29/32"; BHD_E=33 5/8"; D=80 9/16"; D/2=40 9/32"; E=46 15/16"; E+(INLET_RAD+1.5")=71 1/16"; E-(INLET_RAD+1.5")=22 13/16"; F=73 7/8"; F/2=36 15/16"; F/8=9 1/4"; G=34 5/8"; H=3"; INLET_DIA=45 1/4"; INLET_RAD=22 5/8"; INLET_RAD+1.5"=24 1/8"; INLET_RAD/2=11 5/16"; J=3"; J*1.5=4 1/2"; J-.125"=2 7/8"; L=76 3/16"; M=10 1/2"; Model=CA-4 DWDI CCW BHD Class 3; N=2 11/16"; N*2=5 3/8"; N/2=1 11/32"; O=30 21/32"; P=61 5/16"; P/2=30 21/32"; S=22"; T=1 1/16"; T/2=17/32"
- 445_CA-4_DWDI_ARR_3_CCW_BHD_CLASS_1: (B/2)+J=35 1/8"; (F/2)-S=16 3/4"; -(B/2)-J=-35 1/8"; -B=-64 1/4"; -B/2=-32 1/8"; -J*1.5=-4 1/2"; -L+M=-72"; -M=-10 5/8"; A=45 15/16"; A+.25"=46 3/16"; B=64 1/4"; B+.25"=64 1/2"; B/2=32 1/8"; BHD_E=37 1/8"; D=88 11/16"; D/2=44 11/32"; E=51 9/16"; E+(INLET_RAD+1.5")=77 13/16"; E-(INLET_RAD+1.5")=25 5/16"; F=81 1/2"; F/2=40 3/4"; F/8=10 3/16"; G=38 1/4"; H=3"; INLET_DIA=49 1/2"; INLET_RAD=24 3/4"; INLET_RAD+1.5"=26 1/4"; INLET_RAD/2=12 3/8"; J=3"; J*1.5=4 1/2"; J-.125"=2 7/8"; L=82 5/8"; M=10 5/8"; Model=CA-4 DWDI CCW BHD Class 1; N=2 7/16"; N*2=4 7/8"; N/2=1 7/32"; O=33 7/8"; P=67 3/4"; P/2=33 7/8"; S=24"; T=1 1/16"; T/2=17/32"
- 445_CA-4_DWDI_ARR_3_CCW_BHD_CLASS_2: (B/2)+J=35 1/8"; (F/2)-S=16 3/4"; -(B/2)-J=-35 1/8"; -B=-64 1/4"; -B/2=-32 1/8"; -J*1.5=-4 1/2"; -L+M=-72 1/2"; -M=-11"; A=45 15/16"; A+.25"=46 3/16"; B=64 1/4"; B+.25"=64 1/2"; B/2=32 1/8"; BHD_E=37 1/8"; D=88 11/16"; D/2=44 11/32"; E=51 9/16"; E+(INLET_RAD+1.5")=77 13/16"; E-(INLET_RAD+1.5")=25 5/16"; F=81 1/2"; F/2=40 3/4"; F/8=10 3/16"; G=38 1/4"; H=3"; INLET_DIA=49 1/2"; INLET_RAD=24 3/4"; INLET_RAD+1.5"=26 1/4"; INLET_RAD/2=12 3/8"; J=3"; J*1.5=4 1/2"; J-.125"=2 7/8"; L=83 1/2"; M=11"; Model=CA-4 DWDI CCW BHD Class 2; N=2 11/16"; N*2=5 3/8"; N/2=1 11/32"; O=33 7/8"; P=67 3/4"; P/2=33 7/8"; S=24"; T=1 1/16"; T/2=17/32"
- 445_CA-4_DWDI_ARR_3_CCW_BHD_CLASS_3: (B/2)+J=35 1/8"; (F/2)-S=16 3/4"; -(B/2)-J=-35 1/8"; -B=-64 1/4"; -B/2=-32 1/8"; -J*1.5=-4 1/2"; -L+M=-72 1/2"; -M=-11"; A=45 15/16"; A+.25"=46 3/16"; B=64 1/4"; B+.25"=64 1/2"; B/2=32 1/8"; BHD_E=37 1/8"; D=88 11/16"; D/2=44 11/32"; E=51 9/16"; E+(INLET_RAD+1.5")=77 13/16"; E-(INLET_RAD+1.5")=25 5/16"; F=81 1/2"; F/2=40 3/4"; F/8=10 3/16"; G=38 1/4"; H=3"; INLET_DIA=49 1/2"; INLET_RAD=24 3/4"; INLET_RAD+1.5"=26 1/4"; INLET_RAD/2=12 3/8"; J=3"; J*1.5=4 1/2"; J-.125"=2 7/8"; L=83 1/2"; M=11"; Model=CA-4 DWDI CCW BHD Class 3; N=2 15/16"; N*2=5 7/8"; N/2=1 15/32"; O=33 7/8"; P=67 3/4"; P/2=33 7/8"; S=24"; T=1 1/16"; T/2=17/32"
- 490_CA-4_DWDI_ARR_3_CCW_BHD_CLASS_1: (B/2)+J=38 1/16"; (F/2)-S=18 3/8"; -(B/2)-J=-38 1/16"; -B=-70 1/8"; -B/2=-35 1/16"; -J*1.5=-4 1/2"; -L+M=-78"; -M=-11 1/2"; A=51"; A+.25"=51 1/4"; B=70 1/8"; B+.25"=70 3/8"; B/2=35 1/16"; BHD_E=40 3/4"; D=97 3/16"; D/2=48 19/32"; E=56 7/16"; E+(INLET_RAD+1.5")=85 7/16"; E-(INLET_RAD+1.5")=27 7/16"; F=89 3/4"; F/2=44 7/8"; F/8=11 7/32"; G=42 1/4"; H=3"; INLET_DIA=55"; INLET_RAD=27 1/2"; INLET_RAD+1.5"=29"; INLET_RAD/2=13 3/4"; J=3"; J*1.5=4 1/2"; J-.125"=2 7/8"; L=89 1/2"; M=11 1/2"; Model=CA-4 DWDI CCW BHD Class 1; N=2 15/16"; N*2=5 7/8"; N/2=1 15/32"; O=36 13/16"; P=73 5/8"; P/2=36 13/16"; S=26 1/2"; T=1 1/16"; T/2=17/32"
- 490_CA-4_DWDI_ARR_3_CCW_BHD_CLASS_2: (B/2)+J=38 1/16"; (F/2)-S=18 3/8"; -(B/2)-J=-38 1/16"; -B=-70 1/8"; -B/2=-35 1/16"; -J*1.5=-4 1/2"; -L+M=-78 3/8"; -M=-12"; A=51"; A+.25"=51 1/4"; B=70 1/8"; B+.25"=70 3/8"; B/2=35 1/16"; BHD_E=40 3/4"; D=97 3/16"; D/2=48 19/32"; E=56 7/16"; E+(INLET_RAD+1.5")=85 7/16"; E-(INLET_RAD+1.5")=27 7/16"; F=89 3/4"; F/2=44 7/8"; F/8=11 7/32"; G=42 1/4"; H=3"; INLET_DIA=55"; INLET_RAD=27 1/2"; INLET_RAD+1.5"=29"; INLET_RAD/2=13 3/4"; J=3"; J*1.5=4 1/2"; J-.125"=2 7/8"; L=90 3/8"; M=12"; Model=CA-4 DWDI CCW BHD Class 2; N=3 7/16"; N*2=6 7/8"; N/2=1 23/32"; O=36 13/16"; P=73 5/8"; P/2=36 13/16"; S=26 1/2"; T=1 1/16"; T/2=17/32"
- 490_CA-4_DWDI_ARR_3_CCW_BHD_CLASS_3: (B/2)+J=38 1/16"; (F/2)-S=18 3/8"; -(B/2)-J=-38 1/16"; -B=-70 1/8"; -B/2=-35 1/16"; -J*1.5=-4 1/2"; -L+M=-78 5/8"; -M=-12"; A=51"; A+.25"=51 1/4"; B=70 1/8"; B+.25"=70 3/8"; B/2=35 1/16"; BHD_E=40 3/4"; D=97 3/16"; D/2=48 19/32"; E=56 7/16"; E+(INLET_RAD+1.5")=85 7/16"; E-(INLET_RAD+1.5")=27 7/16"; F=89 3/4"; F/2=44 7/8"; F/8=11 7/32"; G=42 1/4"; H=3"; INLET_DIA=55"; INLET_RAD=27 1/2"; INLET_RAD+1.5"=29"; INLET_RAD/2=13 3/4"; J=3"; J*1.5=4 1/2"; J-.125"=2 7/8"; L=90 5/8"; M=12"; Model=CA-4 DWDI CCW BHD Class 3; N=3 7/16"; N*2=6 7/8"; N/2=1 23/32"; O=36 13/16"; P=73 5/8"; P/2=36 13/16"; S=26 1/2"; T=1 1/16"; T/2=17/32"
- 540_CA-4_DWDI_ARR_3_CCW_BHD_CLASS_1: (B/2)+J=41 31/32"; (F/2)-S=20 3/8"; -(B/2)-J=-41 31/32"; -B=-77 15/16"; -B/2=-38 31/32"; -J*1.5=-4 1/2"; -L+M=-85 7/8"; -M=-12 7/16"; A=55 3/4"; A+.25"=56"; B=77 15/16"; B+.25"=78 3/16"; B/2=38 31/32"; BHD_E=44 7/8"; D=106 3/4"; D/2=53 3/8"; E=61 7/8"; E+(INLET_RAD+1.5")=93 3/8"; E-(INLET_RAD+1.5")=30 3/8"; F=98 3/4"; F/2=49 3/8"; F/8=12 11/32"; G=46 1/2"; H=3"; INLET_DIA=60"; INLET_RAD=30"; INLET_RAD+1.5"=31 1/2"; INLET_RAD/2=15"; J=3"; J*1.5=4 1/2"; J-.125"=2 7/8"; L=98 5/16"; M=12 7/16"; Model=CA-4 DWDI CCW BHD Class 1; N=3 7/16"; N*2=6 7/8"; N/2=1 23/32"; O=40 23/32"; P=81 7/16"; P/2=40 23/32"; S=29"; T=1 1/16"; T/2=17/32"
- 540_CA-4_DWDI_ARR_3_CCW_BHD_CLASS_2: (B/2)+J=41 31/32"; (F/2)-S=20 3/8"; -(B/2)-J=-41 31/32"; -B=-77 15/16"; -B/2=-38 31/32"; -J*1.5=-4 1/2"; -L+M=-84 9/16"; -M=-13 3/4"; A=55 3/4"; A+.25"=56"; B=77 15/16"; B+.25"=78 3/16"; B/2=38 31/32"; BHD_E=44 7/8"; D=106 3/4"; D/2=53 3/8"; E=61 7/8"; E+(INLET_RAD+1.5")=93 3/8"; E-(INLET_RAD+1.5")=30 3/8"; F=98 3/4"; F/2=49 3/8"; F/8=12 11/32"; G=46 1/2"; H=3"; INLET_DIA=60"; INLET_RAD=30"; INLET_RAD+1.5"=31 1/2"; INLET_RAD/2=15"; J=3"; J*1.5=4 1/2"; J-.125"=2 7/8"; L=98 5/16"; M=13 3/4"; Model=CA-4 DWDI CCW BHD Class 2; N=3 15/16"; N*2=7 7/8"; N/2=1 31/32"; O=40 23/32"; P=81 7/16"; P/2=40 23/32"; S=29"; T=1 1/16"; T/2=17/32"
- 540_CA-4_DWDI_ARR_3_CCW_BHD_CLASS_3: (B/2)+J=41 31/32"; (F/2)-S=20 3/8"; -(B/2)-J=-41 31/32"; -B=-77 15/16"; -B/2=-38 31/32"; -J*1.5=-4 1/2"; -L+M=-86"; -M=-14 3/16"; A=55 3/4"; A+.25"=56"; B=77 15/16"; B+.25"=78 3/16"; B/2=38 31/32"; BHD_E=44 7/8"; D=106 3/4"; D/2=53 3/8"; E=61 7/8"; E+(INLET_RAD+1.5")=93 3/8"; E-(INLET_RAD+1.5")=30 3/8"; F=98 3/4"; F/2=49 3/8"; F/8=12 11/32"; G=46 1/2"; H=3"; INLET_DIA=60"; INLET_RAD=30"; INLET_RAD+1.5"=31 1/2"; INLET_RAD/2=15"; J=3"; J*1.5=4 1/2"; J-.125"=2 7/8"; L=100 3/16"; M=14 3/16"; Model=CA-4 DWDI CCW BHD Class 3; N=3 15/16"; N*2=7 7/8"; N/2=1 31/32"; O=40 23/32"; P=81 7/16"; P/2=40 23/32"; S=29"; T=1 1/16"; T/2=17/32"
- 600_CA-4_DWDI_ARR_3_CCW_BHD_CLASS_1: (B/2)+J=46 1/8"; (F/2)-S=22 13/16"; -(B/2)-J=-46 1/8"; -B=-86 1/4"; -B/2=-43 1/8"; -J*1.5=-4 1/2"; -L+M=-94 1/2"; -M=-13"; A=62 3/16"; A+.25"=62 7/16"; B=86 1/4"; B+.25"=86 1/2"; B/2=43 1/8"; BHD_E=49 3/4"; D=118 1/8"; D/2=59 1/16"; E=68 3/8"; E+(INLET_RAD+1.5")=102 7/8"; E-(INLET_RAD+1.5")=33 7/8"; F=109 5/8"; F/2=54 13/16"; F/8=13 23/32"; G=51 5/8"; H=3"; INLET_DIA=66"; INLET_RAD=33"; INLET_RAD+1.5"=34 1/2"; INLET_RAD/2=16 1/2"; J=3"; J*1.5=4 1/2"; J-.125"=2 7/8"; L=107 1/2"; M=13"; Model=CA-4 DWDI CCW BHD Class 1; N=3 7/16"; N*2=6 7/8"; N/2=1 23/32"; O=44 7/8"; P=89 3/4"; P/2=44 7/8"; S=32"; T=1 1/16"; T/2=17/32"
- 600_CA-4_DWDI_ARR_3_CCW_BHD_CLASS_2: (B/2)+J=46 1/8"; (F/2)-S=22 13/16"; -(B/2)-J=-46 1/8"; -B=-86 1/4"; -B/2=-43 1/8"; -J*1.5=-4 1/2"; -L+M=-94 1/2"; -M=-14 1/4"; A=62 3/16"; A+.25"=62 7/16"; B=86 1/4"; B+.25"=86 1/2"; B/2=43 1/8"; BHD_E=49 3/4"; D=118 1/8"; D/2=59 1/16"; E=68 3/8"; E+(INLET_RAD+1.5")=102 7/8"; E-(INLET_RAD+1.5")=33 7/8"; F=109 5/8"; F/2=54 13/16"; F/8=13 23/32"; G=51 5/8"; H=3"; INLET_DIA=66"; INLET_RAD=33"; INLET_RAD+1.5"=34 1/2"; INLET_RAD/2=16 1/2"; J=3"; J*1.5=4 1/2"; J-.125"=2 7/8"; L=108 3/4"; M=14 1/4"; Model=CA-4 DWDI CCW BHD Class 2; N=3 15/16"; N*2=7 7/8"; N/2=1 31/32"; O=44 7/8"; P=89 3/4"; P/2=44 7/8"; S=32"; T=1 1/16"; T/2=17/32"
- 600_CA-4_DWDI_ARR_3_CCW_BHD_CLASS_3: (B/2)+J=46 1/8"; (F/2)-S=22 13/16"; -(B/2)-J=-46 1/8"; -B=-86 1/4"; -B/2=-43 1/8"; -J*1.5=-4 1/2"; -L+M=-96"; -M=-14 3/4"; A=62 3/16"; A+.25"=62 7/16"; B=86 1/4"; B+.25"=86 1/2"; B/2=43 1/8"; BHD_E=49 3/4"; D=118 1/8"; D/2=59 1/16"; E=68 3/8"; E+(INLET_RAD+1.5")=102 7/8"; E-(INLET_RAD+1.5")=33 7/8"; F=109 5/8"; F/2=54 13/16"; F/8=13 23/32"; G=51 5/8"; H=3"; INLET_DIA=66"; INLET_RAD=33"; INLET_RAD+1.5"=34 1/2"; INLET_RAD/2=16 1/2"; J=3"; J*1.5=4 1/2"; J-.125"=2 7/8"; L=110 3/4"; M=14 3/4"; Model=CA-4 DWDI CCW BHD Class 3; N=4 7/16"; N*2=8 7/8"; N/2=2 7/32"; O=44 7/8"; P=89 3/4"; P/2=44 7/8"; S=32"; T=1 1/16"; T/2=17/32"

## geometry (parser evidence)
native form markers: Sweep x1
no freeform markers — native parametric forms only
